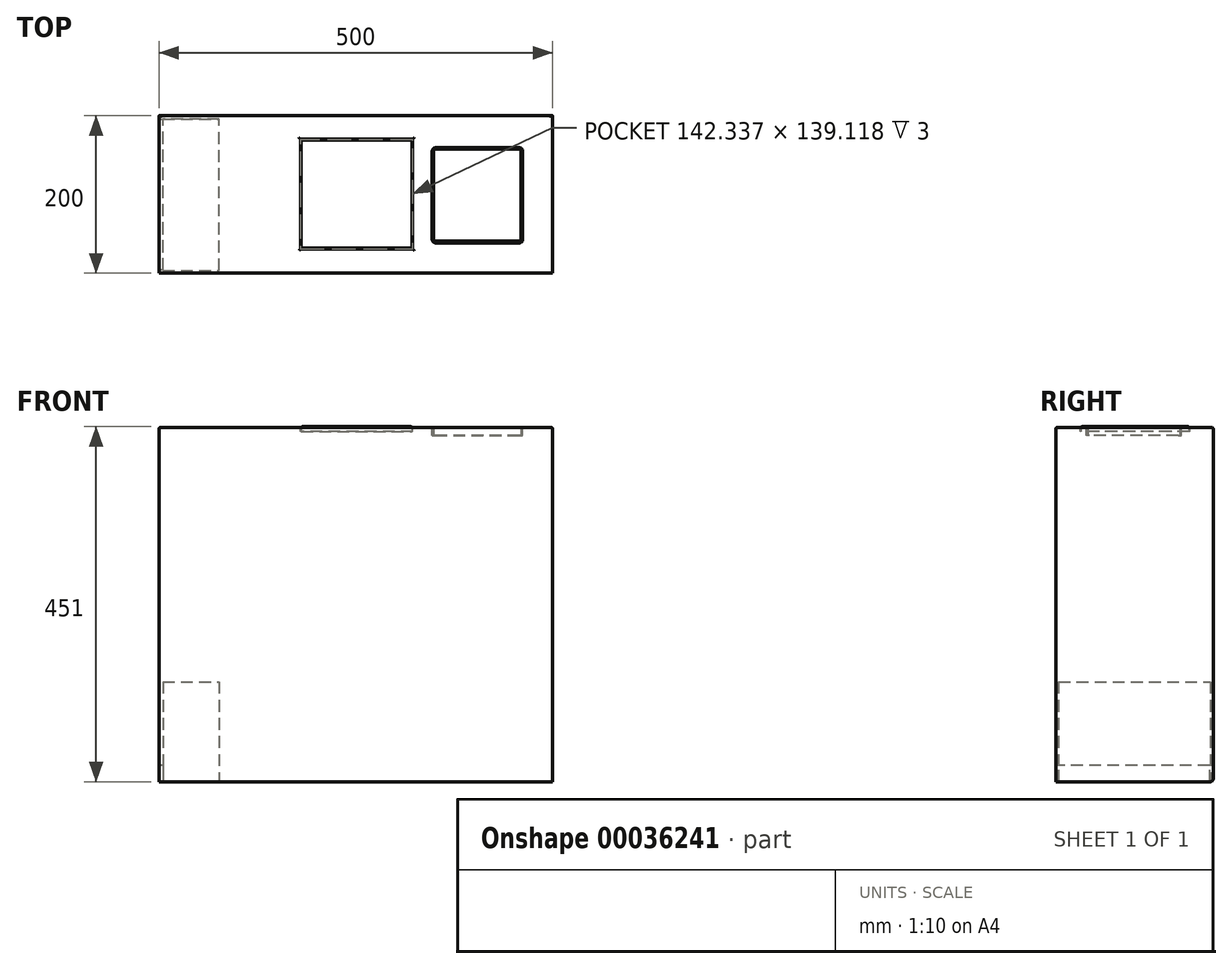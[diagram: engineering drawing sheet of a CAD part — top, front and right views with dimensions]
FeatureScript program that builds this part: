
annotation { "Feature Type Name" : "Feature", "Feature Type Description" : "" }
export const myFeature = defineFeature(function(context is Context, id is Id, definition is map)
    precondition{}
    {
        {
            var Q0;
            Q0=qCreatedBy(makeId("Top.planeOp"),FACE);
            cPlane(context, id + "F0", {"entities" : qUnion([Q0]), "cplaneType" : CPlaneType.OFFSET, "offset" : 50.8 * mm, "width" : 152.4 * mm, "height" : 152.4 * mm});
        }
        {
            var Q0;
            Q0=qCreatedBy(id+"F0.planeOp",FACE);
            var sketch = newSketch(context, id + "F1", { "sketchPlane" : qUnion([Q0])});
            skLineSegment(sketch, "E0.bottom", {"start": v(-233.04, 93.64) * mm, "end": v(266.96, 93.64) * mm});
            skLineSegment(sketch, "E0.top", {"start": v(-233.04, -106.36) * mm, "end": v(266.96, -106.36) * mm});
            skLineSegment(sketch, "E0.left", {"start": v(-233.04, 93.64) * mm, "end": v(-233.04, -106.36) * mm});
            skLineSegment(sketch, "E0.right", {"start": v(266.96, 93.64) * mm, "end": v(266.96, -106.36) * mm});
            skPoint(sketch, "E1.visualSharp", {"position": v(266.96, 93.64) * mm});
            skPoint(sketch, "E2.visualSharp", {"position": v(266.96, -106.36) * mm});
            skPoint(sketch, "E3.visualSharp", {"position": v(-233.04, -106.36) * mm});
            skPoint(sketch, "E4.visualSharp", {"position": v(-233.04, 93.64) * mm});
            skSolve(sketch);
        }
        {
            var Q0;
            Q0=makeQuery(id+"F1.imprint","IMPRINT",FACE,{"disambiguationData":[TD([[makeQuery(id+"F1.imprint","IMPRINT",EDGE,{"derivedFrom":sQuery(id+"F1.wireOp",EDGE,"E0.bottom")}),-1.0]])]});
            extrude(context, id + "F2", {"entities" : qUnion([Q0]), "depth" : 450 * mm});
        }
        {
            var Q0;
            Q0=makeQuery(id+"F2.opExtrude","CAP_FACE",FACE,{"disambiguationData":[OSD([sQuery(id+"F1.wireOp",EDGE,"E0.bottom"),sQuery(id+"F1.wireOp",EDGE,"E0.top"),sQuery(id+"F1.wireOp",EDGE,"E0.left"),sQuery(id+"F1.wireOp",EDGE,"E0.right")])],"isStart":false});
            var sketch = newSketch(context, id + "F3", { "sketchPlane" : qUnion([Q0])});
            skLineSegment(sketch, "E5.bottom", {"start": v(228.86, 53) * mm, "end": v(114.03, 53) * mm});
            skLineSegment(sketch, "E5.top", {"start": v(228.86, -67.78) * mm, "end": v(114.03, -67.78) * mm});
            skLineSegment(sketch, "E5.left", {"start": v(228.86, 53) * mm, "end": v(228.86, -67.78) * mm});
            skLineSegment(sketch, "E5.right", {"start": v(114.03, 53) * mm, "end": v(114.03, -67.78) * mm});
            skSolve(sketch);
        }
        {
            var Q0;
            Q0=makeQuery(id+"F3.imprint","IMPRINT",FACE,{"disambiguationData":[TD([[makeQuery(id+"F3.imprint","IMPRINT",EDGE,{"derivedFrom":sQuery(id+"F3.wireOp",EDGE,"E5.bottom")}),1.0]])]});
            extrude(context, id + "F4", {"entities" : qUnion([Q0]), "operationType" : NewBodyOperationType.REMOVE, "oppositeDirection" : true, "depth" : 10 * mm});
        }
        {
            var Q0;
            Q0=makeQuery(id+"F4.boolean.opBoolean","COPY",EDGE,{"derivedFrom":makeQuery(id+"F4.opExtrude","SWEPT_EDGE",EDGE,{"disambiguationData":[OSD([sQuery(id+"F3.wireOp",EDGE,"E5.bottom"),sQuery(id+"F3.wireOp",EDGE,"E5.left")])]})});
            var Q1;
            Q1=makeQuery(id+"F4.boolean.opBoolean","COPY",EDGE,{"derivedFrom":makeQuery(id+"F4.opExtrude","SWEPT_EDGE",EDGE,{"disambiguationData":[OSD([sQuery(id+"F3.wireOp",EDGE,"E5.top"),sQuery(id+"F3.wireOp",EDGE,"E5.left")])]})});
            var Q2;
            Q2=makeQuery(id+"F2.opExtrude","CAP_EDGE",EDGE,{"disambiguationData":[OSD([sQuery(id+"F1.wireOp",EDGE,"E0.bottom")])],"isStart":true});
            var Q3;
            Q3=makeQuery(id+"F4.boolean.opBoolean","COPY",EDGE,{"derivedFrom":makeQuery(id+"F4.opExtrude","SWEPT_EDGE",EDGE,{"disambiguationData":[OSD([sQuery(id+"F3.wireOp",EDGE,"E5.bottom"),sQuery(id+"F3.wireOp",EDGE,"E5.right")])]})});
            var Q4;
            Q4=makeQuery(id+"F4.boolean.opBoolean","COPY",EDGE,{"derivedFrom":makeQuery(id+"F4.opExtrude","SWEPT_EDGE",EDGE,{"disambiguationData":[OSD([sQuery(id+"F3.wireOp",EDGE,"E5.top"),sQuery(id+"F3.wireOp",EDGE,"E5.right")])]})});
            fillet(context, id + "F5", {"entities" : qUnion([Q0, Q1, Q2, Q3, Q4]), "radius" : 4 * mm, "tangentPropagation" : true, "allowEdgeOverflow" : false});
        }
        {
            var Q0;
            Q0=makeQuery(id+"F4.boolean.opBoolean","COPY",FACE,{"derivedFrom":makeQuery(id+"F4.opExtrude","CAP_FACE",FACE,{"disambiguationData":[OSD([sQuery(id+"F3.wireOp",EDGE,"E5.bottom"),sQuery(id+"F3.wireOp",EDGE,"E5.top"),sQuery(id+"F3.wireOp",EDGE,"E5.left"),sQuery(id+"F3.wireOp",EDGE,"E5.right")])],"isStart":false})});
            var sketch = newSketch(context, id + "F6", { "sketchPlane" : qUnion([Q0])});
            skLineSegment(sketch, "E6.bottom", {"start": v(117.8, 51.22) * mm, "end": v(224.64, 51.22) * mm});
            skLineSegment(sketch, "E6.top", {"start": v(117.8, -65.59) * mm, "end": v(224.64, -65.59) * mm});
            skLineSegment(sketch, "E6.left", {"start": v(115.8, 49.22) * mm, "end": v(115.8, -63.59) * mm});
            skLineSegment(sketch, "E6.right", {"start": v(226.64, 49.22) * mm, "end": v(226.64, -63.59) * mm});
            skPoint(sketch, "E7.visualSharp", {"position": v(115.8, 51.22) * mm});
            skArc(sketch, "E7.filletArc", {"start": v(117.8, 51.22) * mm, "mid": v(116.39, 50.64) * mm, "end": v(115.8, 49.22) * mm});
            skPoint(sketch, "E8.visualSharp", {"position": v(226.64, 51.22) * mm});
            skArc(sketch, "E8.filletArc", {"start": v(226.64, 49.22) * mm, "mid": v(226.05, 50.64) * mm, "end": v(224.64, 51.22) * mm});
            skPoint(sketch, "E9.visualSharp", {"position": v(226.64, -65.59) * mm});
            skArc(sketch, "E9.filletArc", {"start": v(224.64, -65.59) * mm, "mid": v(226.05, -65) * mm, "end": v(226.64, -63.59) * mm});
            skPoint(sketch, "E10.visualSharp", {"position": v(115.8, -65.59) * mm});
            skArc(sketch, "E10.filletArc", {"start": v(115.8, -63.59) * mm, "mid": v(116.39, -65) * mm, "end": v(117.8, -65.59) * mm});
            skSolve(sketch);
        }
        {
            var Q0;
            Q0 = qSketchRegion(id + "F6", true);
            extrude(context, id + "F7", {"entities" : qUnion([Q0]), "depth" : 10 * mm});
        }
        {
            var Q0;
            Q0=makeQuery(id+"F7.opExtrude","CAP_FACE",FACE,{"disambiguationData":[OSD([sQuery(id+"F6.wireOp",EDGE,"E6.bottom"),sQuery(id+"F6.wireOp",EDGE,"E6.top"),sQuery(id+"F6.wireOp",EDGE,"E6.left"),sQuery(id+"F6.wireOp",EDGE,"E6.right"),sQuery(id+"F6.wireOp",EDGE,"E7.filletArc"),sQuery(id+"F6.wireOp",EDGE,"E8.filletArc"),sQuery(id+"F6.wireOp",EDGE,"E9.filletArc"),sQuery(id+"F6.wireOp",EDGE,"E10.filletArc")])],"isStart":false});
            fillet(context, id + "F8", {"entities" : qUnion([Q0]), "radius" : 2 * mm, "tangentPropagation" : true, "allowEdgeOverflow" : false});
        }
        {
            var Q0;
            Q0=makeQuery(id+"F2.opExtrude","CAP_FACE",FACE,{"disambiguationData":[OSD([sQuery(id+"F1.wireOp",EDGE,"E0.bottom"),sQuery(id+"F1.wireOp",EDGE,"E0.top"),sQuery(id+"F1.wireOp",EDGE,"E0.left"),sQuery(id+"F1.wireOp",EDGE,"E0.right")])],"isStart":false});
            var sketch = newSketch(context, id + "F9", { "sketchPlane" : qUnion([Q0])});
            skLineSegment(sketch, "E11.bottom", {"start": v(89.2, 63.74) * mm, "end": v(-53.14, 63.74) * mm});
            skLineSegment(sketch, "E11.top", {"start": v(89.2, -75.38) * mm, "end": v(-53.14, -75.38) * mm});
            skLineSegment(sketch, "E11.left", {"start": v(89.2, 63.74) * mm, "end": v(89.2, -75.38) * mm});
            skLineSegment(sketch, "E11.right", {"start": v(-53.14, 63.74) * mm, "end": v(-53.14, -75.38) * mm});
            skSolve(sketch);
        }
        {
            var Q0;
            Q0=makeQuery(id+"F9.imprint","IMPRINT",FACE,{"disambiguationData":[TD([[makeQuery(id+"F9.imprint","IMPRINT",EDGE,{"derivedFrom":sQuery(id+"F9.wireOp",EDGE,"E11.bottom")}),1.0]])]});
            extrude(context, id + "F10", {"entities" : qUnion([Q0]), "operationType" : NewBodyOperationType.REMOVE, "oppositeDirection" : true, "depth" : 5 * mm});
        }
        {
            var Q0;
            Q0=makeQuery(id+"F10.boolean.opBoolean","COPY",FACE,{"derivedFrom":makeQuery(id+"F10.opExtrude","CAP_FACE",FACE,{"disambiguationData":[OSD([sQuery(id+"F9.wireOp",EDGE,"E11.bottom"),sQuery(id+"F9.wireOp",EDGE,"E11.top"),sQuery(id+"F9.wireOp",EDGE,"E11.left"),sQuery(id+"F9.wireOp",EDGE,"E11.right")])],"isStart":false})});
            var sketch = newSketch(context, id + "F11", { "sketchPlane" : qUnion([Q0])});
            skLineSegment(sketch, "E12.bottom", {"start": v(-52.39, 62.82) * mm, "end": v(88.2, 62.82) * mm});
            skLineSegment(sketch, "E12.top", {"start": v(-52.39, -74.36) * mm, "end": v(88.2, -74.36) * mm});
            skLineSegment(sketch, "E12.left", {"start": v(-52.39, 62.82) * mm, "end": v(-52.39, -74.36) * mm});
            skLineSegment(sketch, "E12.right", {"start": v(88.2, 62.82) * mm, "end": v(88.2, -74.36) * mm});
            skSolve(sketch);
        }
        {
            var Q0;
            Q0=makeQuery(id+"F11.imprint","IMPRINT",FACE,{"disambiguationData":[TD([[makeQuery(id+"F11.imprint","IMPRINT",EDGE,{"derivedFrom":sQuery(id+"F11.wireOp",EDGE,"E12.bottom")}),-1.0]])]});
            extrude(context, id + "F12", {"entities" : qUnion([Q0]), "depth" : 6 * mm});
        }
        {
            var Q0;
            Q0=makeQuery(id+"F12.opExtrude","CAP_FACE",FACE,{"disambiguationData":[OSD([sQuery(id+"F11.wireOp",EDGE,"E12.bottom"),sQuery(id+"F11.wireOp",EDGE,"E12.top"),sQuery(id+"F11.wireOp",EDGE,"E12.left"),sQuery(id+"F11.wireOp",EDGE,"E12.right")])],"isStart":false});
            fillet(context, id + "F13", {"entities" : qUnion([Q0]), "radius" : 1 * mm, "tangentPropagation" : true, "allowEdgeOverflow" : false});
        }
        {
            var Q0;
            Q0=makeQuery(id+"F2.opExtrude","CAP_FACE",FACE,{"disambiguationData":[OSD([sQuery(id+"F1.wireOp",EDGE,"E0.bottom"),sQuery(id+"F1.wireOp",EDGE,"E0.top"),sQuery(id+"F1.wireOp",EDGE,"E0.left"),sQuery(id+"F1.wireOp",EDGE,"E0.right")])],"isStart":false});
            fillet(context, id + "F14", {"entities" : qUnion([Q0]), "radius" : 2 * mm, "tangentPropagation" : true, "allowEdgeOverflow" : false});
        }
        {
            var Q0;
            Q0=makeQuery(id+"F1.imprint","IMPRINT",FACE,{"disambiguationData":[TD([[makeQuery(id+"F1.imprint","IMPRINT",EDGE,{"derivedFrom":sQuery(id+"F1.wireOp",EDGE,"E0.bottom")}),-1.0]])]});
            var sketch = newSketch(context, id + "F15", { "sketchPlane" : qUnion([Q0])});
            skLineSegment(sketch, "E13.bottom", {"start": v(-228.13, -103.02) * mm, "end": v(-156.5, -103.02) * mm});
            skLineSegment(sketch, "E13.top", {"start": v(-228.13, 89.67) * mm, "end": v(-156.5, 89.67) * mm});
            skLineSegment(sketch, "E13.left", {"start": v(-228.13, -103.02) * mm, "end": v(-228.13, 89.67) * mm});
            skLineSegment(sketch, "E13.right", {"start": v(-156.5, -103.02) * mm, "end": v(-156.5, 89.67) * mm});
            skSolve(sketch);
        }
        {
            var Q0;
            Q0=makeQuery(id+"F15.imprint","IMPRINT",FACE,{"disambiguationData":[TD([[makeQuery(id+"F15.imprint","IMPRINT",EDGE,{"derivedFrom":sQuery(id+"F15.wireOp",EDGE,"E13.bottom")}),1.0]])]});
            extrude(context, id + "F16", {"entities" : qUnion([Q0]), "operationType" : NewBodyOperationType.REMOVE, "depth" : 127 * mm});
        }
        {
            var Q0;
            Q0=makeQuery(id+"F2.opExtrude","SWEPT_FACE",FACE,{"disambiguationData":[OSD([sQuery(id+"F1.wireOp",EDGE,"E0.left")])]});
            var sketch = newSketch(context, id + "F17", { "sketchPlane" : qUnion([Q0])});
            skLineSegment(sketch, "E14.bottom", {"start": v(-88.98, 48.7) * mm, "end": v(102.32, 48.7) * mm});
            skLineSegment(sketch, "E14.top", {"start": v(-88.98, 71.38) * mm, "end": v(102.32, 71.38) * mm});
            skLineSegment(sketch, "E14.left", {"start": v(-88.98, 48.7) * mm, "end": v(-88.98, 71.38) * mm});
            skLineSegment(sketch, "E14.right", {"start": v(102.32, 48.7) * mm, "end": v(102.32, 71.38) * mm});
            skPoint(sketch, "E15.oppositeSnap0", {"position": v(-88.98, 60.04) * mm});
            skSolve(sketch);
        }
        {
            var Q0;
            {var subQ3=sQuery(id+"F17.wireOp",EDGE,"E14.bottom");Q0=makeQuery(id+"F17.imprint","IMPRINT",FACE,{"disambiguationData":[TD([[makeQuery(id+"F17.imprint","IMPRINT",EDGE,{"derivedFrom":subQ3}),1.0]])]});}
            var Q1;
            {var subQ3=sQuery(id+"F17.wireOp",EDGE,"E14.top");Q1=makeQuery(id+"F17.imprint","IMPRINT",FACE,{"disambiguationData":[TD([[makeQuery(id+"F17.imprint","IMPRINT",EDGE,{"derivedFrom":subQ3}),-1.0]])]});}
            extrude(context, id + "F18", {"entities" : qUnion([Q0, Q1]), "operationType" : NewBodyOperationType.REMOVE, "endBound" : BoundingType.UP_TO_NEXT, "oppositeDirection" : true, "depth" : 25.4 * mm});
        }
    });
